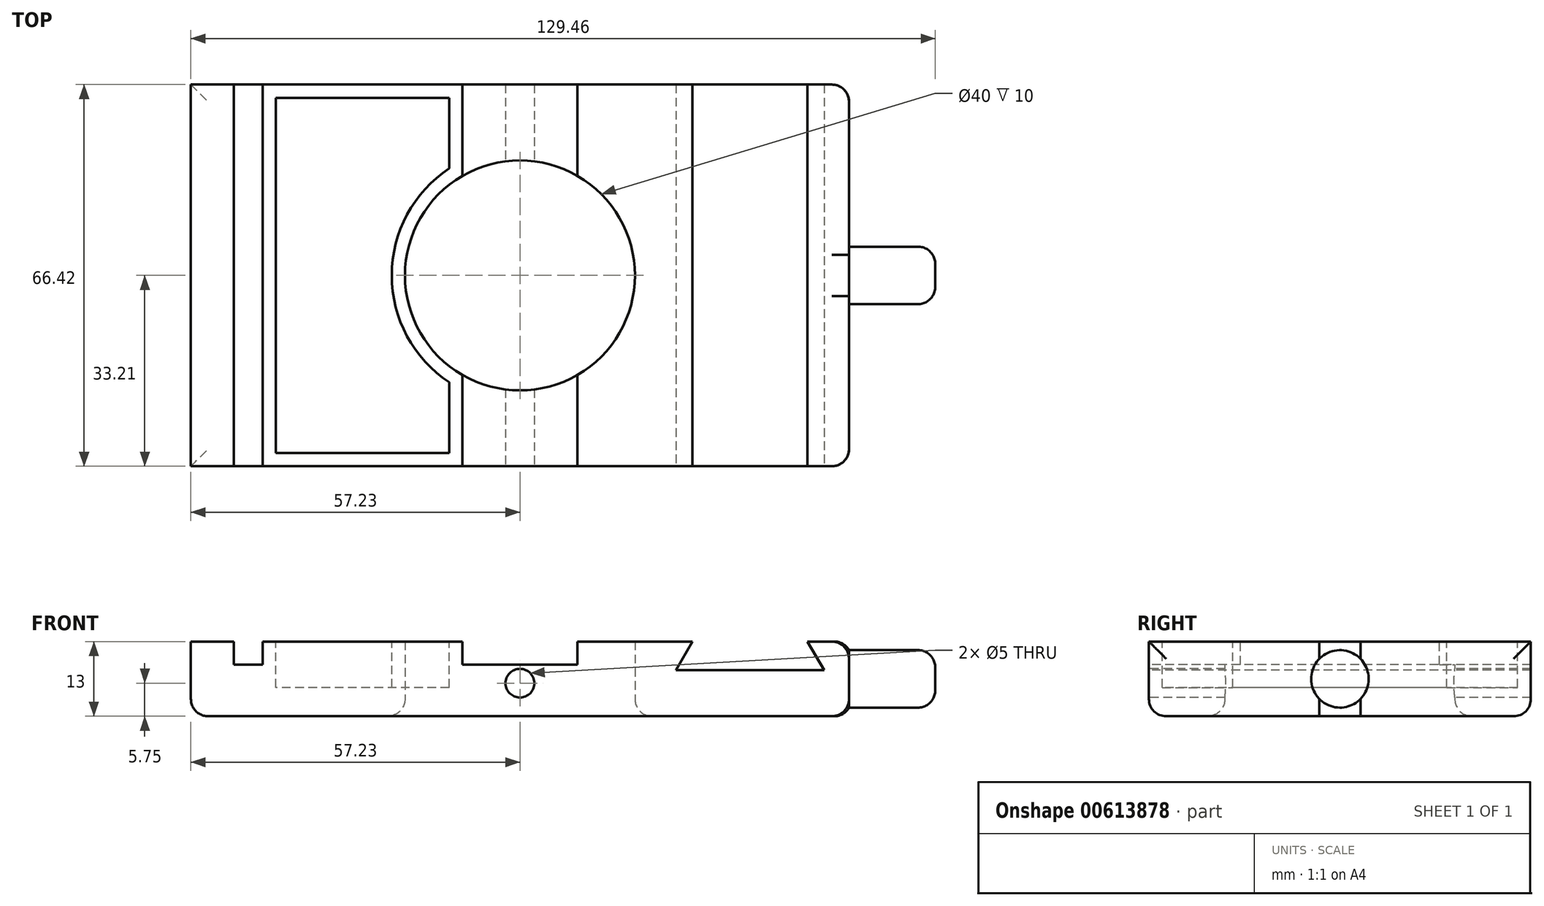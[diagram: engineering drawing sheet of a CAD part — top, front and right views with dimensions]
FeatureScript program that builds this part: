
annotation { "Feature Type Name" : "Feature", "Feature Type Description" : "" }
export const myFeature = defineFeature(function(context is Context, id is Id, definition is map)
    precondition{}
    {
        {
            var Q0;
            Q0=qCreatedBy(makeId("Top.planeOp"),FACE);
            var sketch = newSketch(context, id + "F0", { "sketchPlane" : qUnion([Q0])});
            skLineSegment(sketch, "E0.bottom", {"start": v(-57.23, 33.21) * mm, "end": v(57.23, 33.21) * mm});
            skLineSegment(sketch, "E0.top", {"start": v(-57.23, -33.21) * mm, "end": v(57.23, -33.21) * mm});
            skLineSegment(sketch, "E0.left", {"start": v(-57.23, 33.21) * mm, "end": v(-57.23, -33.21) * mm});
            skLineSegment(sketch, "E0.right", {"start": v(57.23, 33.21) * mm, "end": v(57.23, -33.21) * mm});
            skPoint(sketch, "E0.middle", {"position": v(0, 0) * mm});
            skCircle(sketch, "E1", {"center": v(0, 0) * mm, "radius": 20 * mm});
            skSolve(sketch);
        }
        {
            var Q0;
            Q0=makeQuery(id+"F0.imprint","IMPRINT",FACE,{"disambiguationData":[TD([[makeQuery(id+"F0.imprint","IMPRINT",EDGE,{"derivedFrom":sQuery(id+"F0.wireOp",EDGE,"E0.bottom")}),-1.0]])]});
            extrude(context, id + "F1", {"entities" : qUnion([Q0]), "depth" : 13 * mm, "offsetDistance" : 25 * mm});
        }
        {
            var Q0;
            Q0=makeQuery(id+"F1.opExtrude","CAP_FACE",FACE,{"disambiguationData":[OSD([sQuery(id+"F0.wireOp",EDGE,"E0.bottom"),sQuery(id+"F0.wireOp",EDGE,"E0.top"),sQuery(id+"F0.wireOp",EDGE,"E0.left"),sQuery(id+"F0.wireOp",EDGE,"E0.right"),sQuery(id+"F0.wireOp",EDGE,"E1")])],"isStart":false});
            var sketch = newSketch(context, id + "F2", { "sketchPlane" : qUnion([Q0])});
            skLineSegment(sketch, "E2.bottom", {"start": v(-49.74, 33.21) * mm, "end": v(-44.74, 33.21) * mm});
            skLineSegment(sketch, "E2.top", {"start": v(-49.74, -33.21) * mm, "end": v(-44.74, -33.21) * mm});
            skLineSegment(sketch, "E2.left", {"start": v(-49.74, 33.21) * mm, "end": v(-49.74, -33.21) * mm});
            skLineSegment(sketch, "E2.right", {"start": v(-44.74, 33.21) * mm, "end": v(-44.74, -33.21) * mm});
            skLineSegment(sketch, "E3", {"start": v(10, 33.21) * mm, "end": v(10, -33.21) * mm});
            skLineSegment(sketch, "E4", {"start": v(10, -33.21) * mm, "end": v(-10, -33.21) * mm});
            skLineSegment(sketch, "E5", {"start": v(-10, -33.21) * mm, "end": v(-10, 33.21) * mm});
            skPoint(sketch, "E6", {"position": v(0, 0) * mm});
            skPoint(sketch, "E7", {"position": v(0, -33.21) * mm});
            skPoint(sketch, "E8", {"position": v(0, 33.21) * mm});
            skLineSegment(sketch, "E9", {"start": v(0, 33.21) * mm, "end": v(0, -33.21) * mm, "construction": true});
            skSolve(sketch);
        }
        {
            var Q0;
            Q0=makeQuery(id+"F2.imprint","IMPRINT",FACE,{"disambiguationData":[TD([[makeQuery(id+"F2.imprint","IMPRINT",EDGE,{"derivedFrom":sQuery(id+"F2.wireOp",EDGE,"E2.bottom")}),-1.0]])]});
            var Q1;
            {var subQ0=sQuery(id+"F2.wireOp",EDGE,"E4");Q1=makeQuery(id+"F2.imprint","IMPRINT",FACE,{"disambiguationData":[TD([[makeQuery(id+"F2.imprint","IMPRINT",EDGE,{"derivedFrom":subQ0}),1.0]])]});}
            var Q2;
            {var subQ0=sQuery(id+"F2.wireOp",EDGE,"E3");var subQ1=makeQuery(id+"F1.opExtrude","CAP_EDGE",EDGE,{"disambiguationData":[OSD([sQuery(id+"F0.wireOp",EDGE,"E0.bottom")])],"isStart":false});var subQ2=makeQuery(id+"F2.imprint","INTERSECT",VERTEX,{"derivedFrom":[subQ1,subQ0]});Q2=makeQuery(id+"F2.imprint","IMPRINT",FACE,{"disambiguationData":[TD([[makeQuery(id+"F2.imprint","IMPRINT",EDGE,{"disambiguationData":[TD([[subQ2,-1.0]])],"derivedFrom":subQ0}),-1.0]])]});}
            extrude(context, id + "F3", {"entities" : qUnion([Q0, Q1, Q2]), "operationType" : NewBodyOperationType.REMOVE, "oppositeDirection" : true, "depth" : 4 * mm, "offsetDistance" : 25 * mm});
        }
        {
            var Q0;
            Q0=makeQuery(id+"F1.opExtrude","SWEPT_FACE",FACE,{"disambiguationData":[OSD([sQuery(id+"F0.wireOp",EDGE,"E0.top")])]});
            var sketch = newSketch(context, id + "F4", { "sketchPlane" : qUnion([Q0])});
            skLineSegment(sketch, "E10", {"start": v(30, 13) * mm, "end": v(27.11, 8) * mm});
            skLineSegment(sketch, "E11", {"start": v(27.11, 8) * mm, "end": v(52.89, 8) * mm});
            skLineSegment(sketch, "E12", {"start": v(52.89, 8) * mm, "end": v(50, 13) * mm});
            skLineSegment(sketch, "E13", {"start": v(50, 13) * mm, "end": v(30, 13) * mm});
            skLineSegment(sketch, "E14", {"start": v(40, 8) * mm, "end": v(40, 18.35) * mm, "construction": true});
            skSolve(sketch);
        }
        {
            var Q0;
            Q0=makeQuery(id+"F4.imprint","IMPRINT",FACE,{"disambiguationData":[TD([[makeQuery(id+"F4.imprint","IMPRINT",EDGE,{"derivedFrom":sQuery(id+"F4.wireOp",EDGE,"E10")}),1.0]])]});
            extrude(context, id + "F5", {"entities" : qUnion([Q0]), "operationType" : NewBodyOperationType.REMOVE, "endBound" : BoundingType.THROUGH_ALL, "oppositeDirection" : true, "depth" : 25 * mm, "offsetDistance" : 25 * mm});
        }
        {
            var Q0;
            Q0=makeQuery(id+"F1.opExtrude","SWEPT_FACE",FACE,{"disambiguationData":[OSD([sQuery(id+"F0.wireOp",EDGE,"E0.top")])]});
            var sketch = newSketch(context, id + "F6", { "sketchPlane" : qUnion([Q0])});
            skLineSegment(sketch, "E15", {"start": v(0, 9) * mm, "end": v(0, 0) * mm, "construction": true});
            skCircle(sketch, "E16", {"center": v(0, 5.75) * mm, "radius": 2.5 * mm});
            skSolve(sketch);
        }
        {
            var Q0;
            Q0=makeQuery(id+"F1.opExtrude","SWEPT_FACE",FACE,{"disambiguationData":[OSD([sQuery(id+"F0.wireOp",EDGE,"E0.right")])]});
            var sketch = newSketch(context, id + "F7", { "sketchPlane" : qUnion([Q0])});
            skPoint(sketch, "E17", {"position": v(0, 6.5) * mm});
            skPoint(sketch, "E17.positionSnap0", {"position": v(-33.21, 6.5) * mm});
            skPoint(sketch, "E17.positionSnap1", {"position": v(0, 13) * mm});
            skCircle(sketch, "E18", {"center": v(0, 6.5) * mm, "radius": 5 * mm});
            skSolve(sketch);
        }
        {
            var Q0;
            Q0=makeQuery(id+"F7.imprint","IMPRINT",FACE,{"disambiguationData":[TD([[makeQuery(id+"F7.imprint","IMPRINT",EDGE,{"derivedFrom":sQuery(id+"F7.wireOp",EDGE,"E18")}),1.0]])]});
            extrude(context, id + "F8", {"entities" : qUnion([Q0]), "operationType" : NewBodyOperationType.ADD, "depth" : 15 * mm, "offsetDistance" : 25 * mm});
        }
        {
            var Q0;
            Q0=makeQuery(id+"F6.imprint","IMPRINT",FACE,{"disambiguationData":[TD([[makeQuery(id+"F6.imprint","IMPRINT",EDGE,{"derivedFrom":sQuery(id+"F6.wireOp",EDGE,"E16")}),1.0]])]});
            extrude(context, id + "F9", {"entities" : qUnion([Q0]), "operationType" : NewBodyOperationType.REMOVE, "endBound" : BoundingType.THROUGH_ALL, "oppositeDirection" : true, "depth" : 25 * mm, "offsetDistance" : 25 * mm});
        }
        {
            var Q0;
            Q0=makeQuery(id+"F1.opExtrude","CAP_EDGE",EDGE,{"disambiguationData":[OSD([sQuery(id+"F0.wireOp",EDGE,"E0.left")])],"isStart":true});
            var Q1;
            Q1=makeQuery(id+"F1.opExtrude","CAP_EDGE",EDGE,{"disambiguationData":[OSD([sQuery(id+"F0.wireOp",EDGE,"E0.right")])],"isStart":true});
            var Q2;
            Q2=makeQuery(id+"F1.opExtrude","CAP_EDGE",EDGE,{"disambiguationData":[OSD([sQuery(id+"F0.wireOp",EDGE,"E0.bottom")])],"isStart":true});
            var Q3;
            Q3=makeQuery(id+"F1.opExtrude","CAP_EDGE",EDGE,{"disambiguationData":[OSD([sQuery(id+"F0.wireOp",EDGE,"E0.top")])],"isStart":true});
            var Q4;
            Q4=makeQuery(id+"F1.opExtrude","CAP_EDGE",EDGE,{"disambiguationData":[OSD([sQuery(id+"F0.wireOp",EDGE,"E1")])],"isStart":true});
            var Q5;
            Q5=makeQuery(id+"F8.opExtrude","CAP_EDGE",EDGE,{"disambiguationData":[OSD([sQuery(id+"F7.wireOp",EDGE,"E18")])],"isStart":false});
            var Q6;
            Q6=makeQuery(id+"F1.opExtrude","CAP_EDGE",EDGE,{"disambiguationData":[OSD([sQuery(id+"F0.wireOp",EDGE,"E0.right")])],"isStart":false});
            var Q7;
            Q7=makeQuery(id+"F1.opExtrude","SWEPT_EDGE",EDGE,{"disambiguationData":[OSD([sQuery(id+"F0.wireOp",EDGE,"E0.bottom"),sQuery(id+"F0.wireOp",EDGE,"E0.right")])]});
            var Q8;
            Q8=makeQuery(id+"F1.opExtrude","SWEPT_EDGE",EDGE,{"disambiguationData":[OSD([sQuery(id+"F0.wireOp",EDGE,"E0.top"),sQuery(id+"F0.wireOp",EDGE,"E0.right")])]});
            fillet(context, id + "F10", {"entities" : qUnion([Q0, Q1, Q2, Q3, Q4, Q5, Q6, Q7, Q8]), "radius" : 3 * mm, "tangentPropagation" : true, "allowEdgeOverflow" : false});
        }
        {
            var Q0;
            {var subQ0=sQuery(id+"F0.wireOp",EDGE,"E1");var subQ1=sQuery(id+"F0.wireOp",EDGE,"E0.top");var subQ4=sQuery(id+"F0.wireOp",EDGE,"E0.bottom");Q0=makeQuery(id+"F3.boolean.opBoolean","SPLIT",FACE,{"disambiguationData":[TD([makeQuery(id+"F3.opExtrude","SWEPT_FACE",FACE,{"disambiguationData":[OSD([sQuery(id+"F2.wireOp",EDGE,"E2.right")])]})])],"derivedFrom":makeQuery(id+"F1.opExtrude","CAP_FACE",FACE,{"disambiguationData":[OSD([subQ4,subQ1,sQuery(id+"F0.wireOp",EDGE,"E0.left"),sQuery(id+"F0.wireOp",EDGE,"E0.right"),subQ0])],"isStart":false})});}
            var sketch = newSketch(context, id + "F11", { "sketchPlane" : qUnion([Q0])});
            skLineSegment(sketch, "E19.0", {"start": v(-12.3, 18.6) * mm, "end": v(-12.3, 30.91) * mm});
            skLineSegment(sketch, "E19.1", {"start": v(-42.44, 30.91) * mm, "end": v(-42.44, -30.91) * mm});
            skLineSegment(sketch, "E19.2", {"start": v(-42.44, -30.91) * mm, "end": v(-12.3, -30.91) * mm});
            skLineSegment(sketch, "E19.3", {"start": v(-12.3, 30.91) * mm, "end": v(-42.44, 30.91) * mm});
            skLineSegment(sketch, "E19.4", {"start": v(-12.3, -30.91) * mm, "end": v(-12.3, -18.6) * mm});
            skArc(sketch, "E19.5", {"start": v(-12.3, -18.6) * mm, "mid": v(-22.3, 0) * mm, "end": v(-12.3, 18.6) * mm});
            skSolve(sketch);
        }
        {
            var Q0;
            Q0=makeQuery(id+"F11.imprint","IMPRINT",FACE,{"disambiguationData":[TD([[makeQuery(id+"F11.imprint","IMPRINT",EDGE,{"derivedFrom":sQuery(id+"F11.wireOp",EDGE,"E19.0")}),1.0]])]});
            extrude(context, id + "F12", {"entities" : qUnion([Q0]), "operationType" : NewBodyOperationType.REMOVE, "oppositeDirection" : true, "depth" : 8 * mm, "offsetDistance" : 25 * mm});
        }
    });
